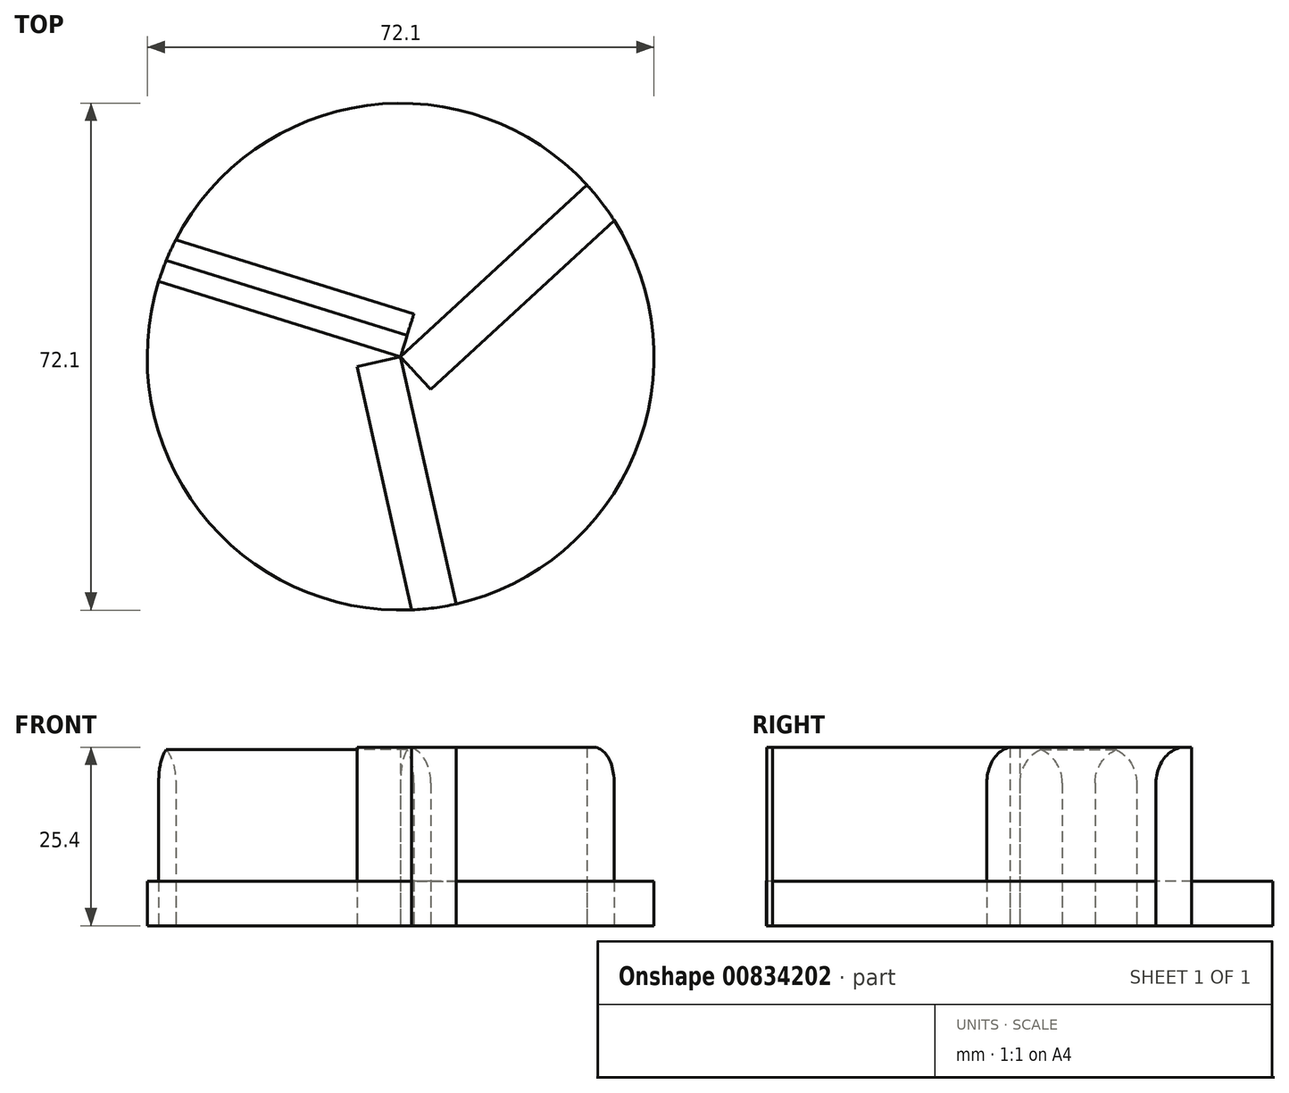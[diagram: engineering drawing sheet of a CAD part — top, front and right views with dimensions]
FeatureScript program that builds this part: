
annotation { "Feature Type Name" : "Feature", "Feature Type Description" : "" }
export const myFeature = defineFeature(function(context is Context, id is Id, definition is map)
    precondition{}
    {
        {
            var Q0;
            Q0=qCreatedBy(makeId("Top.planeOp"),FACE);
            var sketch = newSketch(context, id + "F0", { "sketchPlane" : qUnion([Q0])});
            skCircle(sketch, "E0", {"center": v(0, 0) * mm, "radius": 36.05 * mm});
            skLineSegment(sketch, "E1", {"start": v(0, 0) * mm, "end": v(26.5, 24.44) * mm});
            skLineSegment(sketch, "E2.0", {"start": v(4.3, -4.67) * mm, "end": v(30.4, 19.39) * mm});
            skLineSegment(sketch, "E3", {"start": v(4.3, -4.67) * mm, "end": v(0, 0) * mm});
            skLineSegment(sketch, "E4.1.0", {"start": v(1.9, 6.06) * mm, "end": v(-31.99, 16.63) * mm});
            skLineSegment(sketch, "E4.1.1", {"start": v(0, 0) * mm, "end": v(-34.42, 10.74) * mm});
            skLineSegment(sketch, "E4.1.2", {"start": v(1.9, 6.06) * mm, "end": v(0, 0) * mm});
            skLineSegment(sketch, "E4.2.0", {"start": v(-6.2, -1.4) * mm, "end": v(1.6, -36.02) * mm});
            skLineSegment(sketch, "E4.2.1", {"start": v(0, 0) * mm, "end": v(7.91, -35.17) * mm});
            skLineSegment(sketch, "E4.2.2", {"start": v(-6.2, -1.4) * mm, "end": v(0, 0) * mm});
            skSolve(sketch);
        }
        {
            var Q0;
            {var subQ0=sQuery(id+"F0.wireOp",EDGE,"E4.1.0");Q0=makeQuery(id+"F0.imprint","IMPRINT",FACE,{"disambiguationData":[TD([[makeQuery(id+"F0.imprint","IMPRINT",EDGE,{"derivedFrom":subQ0}),1.0]])]});}
            var Q1;
            {var subQ0=sQuery(id+"F0.wireOp",EDGE,"E4.2.0");Q1=makeQuery(id+"F0.imprint","IMPRINT",FACE,{"disambiguationData":[TD([[makeQuery(id+"F0.imprint","IMPRINT",EDGE,{"derivedFrom":subQ0}),1.0]])]});}
            var Q2;
            {var subQ0=sQuery(id+"F0.wireOp",EDGE,"E1");Q2=makeQuery(id+"F0.imprint","IMPRINT",FACE,{"disambiguationData":[TD([[makeQuery(id+"F0.imprint","IMPRINT",EDGE,{"derivedFrom":subQ0}),-1.0]])]});}
            extrude(context, id + "F1", {"entities" : qUnion([Q0, Q1, Q2]), "depth" : 25.4 * mm, "offsetDistance" : 25.4 * mm});
        }
        {
            var Q0;
            {var subQ0=sQuery(id+"F0.wireOp",EDGE,"E4.1.1");Q0=makeQuery(id+"F0.imprint","IMPRINT",FACE,{"disambiguationData":[TD([[makeQuery(id+"F0.imprint","IMPRINT",EDGE,{"derivedFrom":subQ0}),1.0]])]});}
            var Q1;
            {var subQ0=sQuery(id+"F0.wireOp",EDGE,"E2.0");Q1=makeQuery(id+"F0.imprint","IMPRINT",FACE,{"disambiguationData":[TD([[makeQuery(id+"F0.imprint","IMPRINT",EDGE,{"derivedFrom":subQ0}),-1.0]])]});}
            var Q2;
            {var subQ0=sQuery(id+"F0.wireOp",EDGE,"E1");Q2=makeQuery(id+"F0.imprint","IMPRINT",FACE,{"disambiguationData":[TD([[makeQuery(id+"F0.imprint","IMPRINT",EDGE,{"derivedFrom":subQ0}),1.0]])]});}
            extrude(context, id + "F2", {"entities" : qUnion([Q0, Q1, Q2]), "depth" : 6.35 * mm, "offsetDistance" : 25.4 * mm});
        }
        {
            var Q0;
            Q0=makeQuery(id+"F1.opExtrude","CAP_EDGE",EDGE,{"disambiguationData":[OSD([sQuery(id+"F0.wireOp",EDGE,"E4.1.1")])],"isStart":false});
            var Q1;
            Q1=makeQuery(id+"F1.opExtrude","CAP_EDGE",EDGE,{"disambiguationData":[OSD([sQuery(id+"F0.wireOp",EDGE,"E2.0")])],"isStart":false});
            var Q2;
            Q2=makeQuery(id+"F1.opExtrude","CAP_EDGE",EDGE,{"disambiguationData":[OSD([sQuery(id+"F0.wireOp",EDGE,"E4.1.0")])],"isStart":false});
            fillet(context, id + "F3", {"entities" : qUnion([Q0, Q1, Q2]), "radius" : 5.08 * mm, "tangentPropagation" : true, "allowEdgeOverflow" : false});
        }
    });
